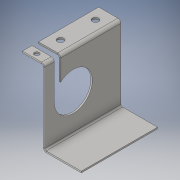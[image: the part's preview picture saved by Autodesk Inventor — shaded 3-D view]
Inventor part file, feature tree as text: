
AUTODESK INVENTOR PART (.ipt)
format: ipt  version: 2016 (Build 200138000, 138)  size: 202,752 bytes
history: native  units: in
note: dims shown in document units (in); Inventor stores cm internally (conversion verified against a paired STEP export)
features: sketch x9, other x8, sheet_metal_op x7
ambient origin geometry x8: Origin, YZ Plane, XZ Plane, XY Plane, X Axis, Y Axis, Z Axis, Center Point
bodies: Solid1 (feature_tree)
feature tree (24):
  sheet_metal_op  "Face1"
  sheet_metal_op  "Flange1"
  sheet_metal_op  "Flange3"
  sketch  "Sketch10"  dims[d7=6.0in d8=90.0deg d9=0.12in]
  sketch  "Sketch1"  dims[d0=6.0in]
  other  "Plate1"
  sketch  "Sketch2"  dims[d1=3.0in]
  other  "Plate2"
  sheet_metal_op  "Bend1"
  sheet_metal_op  "Corner1"
  sketch  "Sketch5"  dims[d2=0.12in]
  sketch  "Sketch6"  dims[d3=0.12in]
  sketch  "Sketch7"  dims[d4=0.06in]
  other  "Plate4"
  sheet_metal_op  "Bend3"
  sheet_metal_op  "Corner3"
  sketch  "Sketch8"  dims[d5=0.24in]
  sketch  "Sketch9"  dims[d6=0.12in]
  sketch  "Sketch11"  dims[d10=0.48in d11=0.12in d12=0.12in d23=3.0in d24=3.0in d25=3.75in d26=0.12in d27=0.0in d28=0.12in d29=0.0in d30=0.12in d31=0.06in d32=0.24in d33=0.12in d34=1.75in d35=90.0deg d36=0.12in d37=0.48in d38=0.12in d39=0.12in d40=0.5in d41=2.75in d42=1.0in d43=0.75in d44=0.75in d45=0.12in d46=0.0in d47=0.5in d48=0.375in d49=0.375in d50=0.75in d51=0.12in d52=0.0in d53=0.25in d54=0.25in d55=0.375in d56=0.375in d57=1.5in d58=0.75in d59=0.25in d60=0.25in d63=1.5in d65=0.375in d66=0.375in d67=0.75in d68=0.12in d69=0.0in]
  other  "Cut1"
  other  "Cut2"
  other  "Cut3"
  other  "Cut4"
  other  "Cut5"
